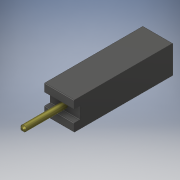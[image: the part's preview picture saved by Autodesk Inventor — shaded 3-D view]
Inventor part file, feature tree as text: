
AUTODESK INVENTOR PART (.ipt)
format: ipt  version: 2017.3 (Build 213257000, 257)  size: 245,248 bytes
history: native  units: mm
features: plane x6, sketch x5, extrude x3, chamfer x2, fillet x1, other x1, sweep x1
ambient origin geometry x8: Origin, YZ Plane, XZ Plane, XY Plane, X Axis, Y Axis, Z Axis, Center Point
bodies: Volumenkörper1 (feature_tree)
feature tree (19):
  extrude  "Extrusion1"  Depth=2.4mm
  extrude  "Extrusion2"  Depth=0.6mm
  chamfer  "Fase1"  Distance=6.5mm
  extrude  "Extrusion4"  Depth=0.6mm TaperAngle=45.0deg
  fillet  "Rundung1"  Radius=0.5mm
  plane  "Arbeitsebene1"
  other  "Trennen1"
  plane  "Arbeitsebene2"
  sweep  "Sweeping1"
  chamfer  "Fase3"  Distance=0.3mm
  plane  "Arbeitsebene5"
  plane  "Arbeitsebene6"
  sketch  "Skizze1"  dims[d0=2.54mm d1=2.4mm]
  sketch  "Skizze2"  dims[d2=8.5mm d3=0.0mm d4=0.6mm]
  sketch  "Skizze3"  dims[d5=0.6mm]
  sketch  "Skizze4"  dims[d6=0.9mm]
  sketch  "Skizze5"  dims[d7=0.97mm d8=6.5mm d9=0.0mm d10=0.6mm d11=2.0mm d12=45.0deg d13=0.5mm d14=0.3mm d15=0.3mm d18=1.0mm d19=0.7mm d20=0.5mm d21=0.0mm d25=0.05mm d26=-1.0mm d27=-1.27mm d28=3.7mm d29=90.0deg d30=0.0mm d31=0.0mm d32=0.15mm d33=2.0mm d34=45.0deg d35=90.0deg d36=90.0deg]
  plane  "Arbeitsebene3"
  plane  "Arbeitsebene4"
